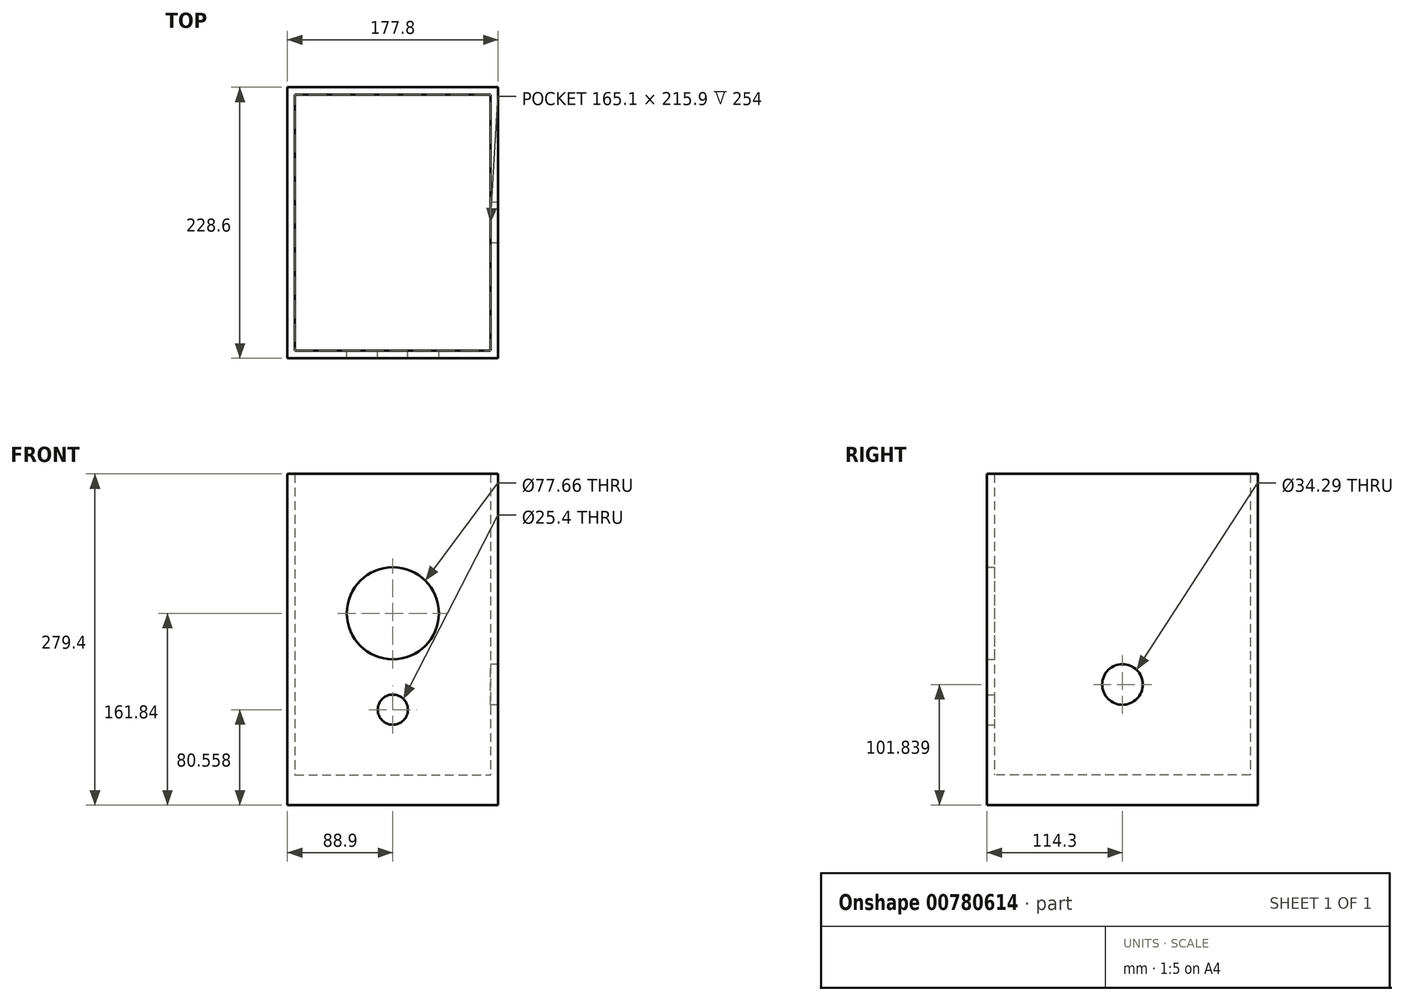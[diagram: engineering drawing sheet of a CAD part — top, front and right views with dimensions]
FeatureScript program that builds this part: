
annotation { "Feature Type Name" : "Feature", "Feature Type Description" : "" }
export const myFeature = defineFeature(function(context is Context, id is Id, definition is map)
    precondition{}
    {
        {
            var Q0;
            Q0=qCreatedBy(makeId("Top.planeOp"),FACE);
            var sketch = newSketch(context, id + "F0", { "sketchPlane" : qUnion([Q0])});
            skLineSegment(sketch, "E0.bottom", {"start": v(-88.9, 114.3) * mm, "end": v(88.9, 114.3) * mm});
            skLineSegment(sketch, "E0.top", {"start": v(-88.9, -114.3) * mm, "end": v(88.9, -114.3) * mm});
            skLineSegment(sketch, "E0.left", {"start": v(-88.9, 114.3) * mm, "end": v(-88.9, -114.3) * mm});
            skLineSegment(sketch, "E0.right", {"start": v(88.9, 114.3) * mm, "end": v(88.9, -114.3) * mm});
            skPoint(sketch, "E0.middle", {"position": v(0, 0) * mm});
            skLineSegment(sketch, "E1.0", {"start": v(-82.55, 107.95) * mm, "end": v(82.55, 107.95) * mm});
            skLineSegment(sketch, "E1.1", {"start": v(-82.55, 107.95) * mm, "end": v(-82.55, -107.95) * mm});
            skLineSegment(sketch, "E1.2", {"start": v(-82.55, -107.95) * mm, "end": v(82.55, -107.95) * mm});
            skLineSegment(sketch, "E1.3", {"start": v(82.55, 107.95) * mm, "end": v(82.55, -107.95) * mm});
            skSolve(sketch);
        }
        {
            var Q0;
            Q0 = qSketchRegion(id + "F0", true);
            extrude(context, id + "F1", {"entities" : qUnion([Q0]), "depth" : 279.4 * mm, "offsetDistance" : 25.4 * mm});
        }
        {
            var Q0;
            Q0=qCreatedBy(makeId("Front.planeOp"),FACE);
            var sketch = newSketch(context, id + "F2", { "sketchPlane" : qUnion([Q0])});
            skCircle(sketch, "E2", {"center": v(0, 80.56) * mm, "radius": 12.7 * mm});
            skCircle(sketch, "E3", {"center": v(0, 161.84) * mm, "radius": 38.83 * mm});
            skSolve(sketch);
        }
        {
            var Q0;
            Q0 = qSketchRegion(id + "F2", true);
            extrude(context, id + "F3", {"entities" : qUnion([Q0]), "operationType" : NewBodyOperationType.REMOVE, "depth" : 254 * mm, "offsetDistance" : 25.4 * mm});
        }
        {
            var Q0;
            Q0=qCreatedBy(makeId("Right.planeOp"),FACE);
            var sketch = newSketch(context, id + "F4", { "sketchPlane" : qUnion([Q0])});
            skCircle(sketch, "E4", {"center": v(0, 101.84) * mm, "radius": 17.15 * mm});
            skSolve(sketch);
        }
        {
            var Q0;
            Q0 = qSketchRegion(id + "F4", true);
            extrude(context, id + "F5", {"entities" : qUnion([Q0]), "operationType" : NewBodyOperationType.REMOVE, "depth" : 254 * mm, "offsetDistance" : 25.4 * mm});
        }
        {
            var Q0;
            Q0=makeQuery(id+"F0.imprint","IMPRINT",FACE,{"disambiguationData":[TD([[makeQuery(id+"F0.imprint","IMPRINT",EDGE,{"derivedFrom":sQuery(id+"F0.wireOp",EDGE,"E1.0")}),-1.0]])]});
            extrude(context, id + "F6", {"entities" : qUnion([Q0]), "operationType" : NewBodyOperationType.ADD, "depth" : 25.4 * mm, "offsetDistance" : 25.4 * mm});
        }
    });
